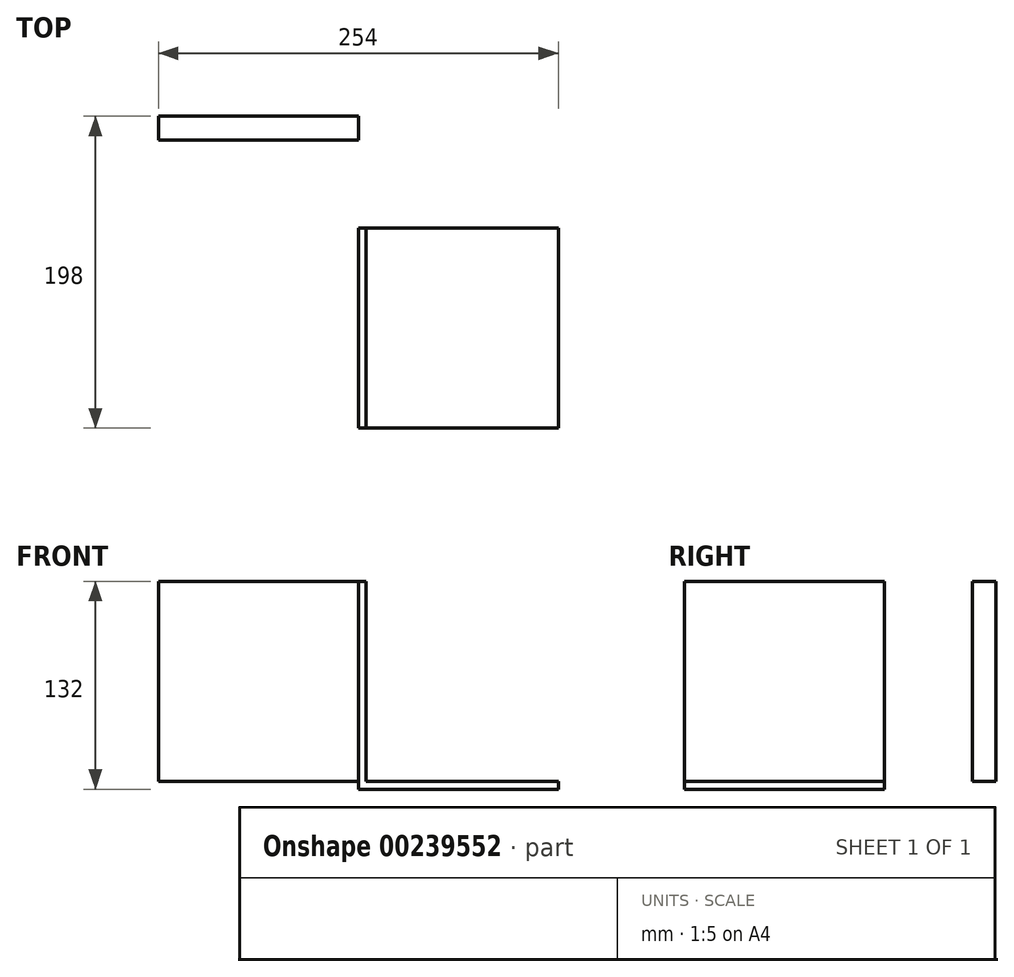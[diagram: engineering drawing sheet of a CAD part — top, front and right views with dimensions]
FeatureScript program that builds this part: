
annotation { "Feature Type Name" : "Feature", "Feature Type Description" : "" }
export const myFeature = defineFeature(function(context is Context, id is Id, definition is map)
    precondition{}
    {
        {
            assignVariable(context, id + "F0", {"name" : "L", "anyValue" : 5});
        }
        {
            var Q0;
            Q0=qCreatedBy(makeId("Front.planeOp"),FACE);
            var sketch = newSketch(context, id + "F1", { "sketchPlane" : qUnion([Q0])});
            skLineSegment(sketch, "E0.bottom", {"start": v(63.5, 63.5) * mm, "end": v(-63.5, 63.5) * mm});
            skLineSegment(sketch, "E0.top", {"start": v(63.5, -63.5) * mm, "end": v(-63.5, -63.5) * mm});
            skLineSegment(sketch, "E0.left", {"start": v(63.5, 63.5) * mm, "end": v(63.5, -63.5) * mm});
            skLineSegment(sketch, "E0.right", {"start": v(-63.5, 63.5) * mm, "end": v(-63.5, -63.5) * mm});
            skPoint(sketch, "E0.middle", {"position": v(0, 0) * mm});
            skSolve(sketch);
        }
        {
            var Q0;
            Q0 = qSketchRegion(id + "F1", true);
            extrude(context, id + "F2", {"entities" : qUnion([Q0]), "endBound" : BoundingType.SYMMETRIC, "depth" : (getVariable(context, 'L') * 3) * mm});
        }
        {
            var Q0;
            Q0=makeQuery(id+"F2.opExtrude","SWEPT_FACE",FACE,{"disambiguationData":[OSD([sQuery(id+"F1.wireOp",EDGE,"E0.left")])]});
            var sketch = newSketch(context, id + "F3", { "sketchPlane" : qUnion([Q0])});
            skLineSegment(sketch, "E1.bottom", {"start": v(-190.5, 63.5) * mm, "end": v(-63.5, 63.5) * mm});
            skLineSegment(sketch, "E1.top", {"start": v(-190.5, -63.5) * mm, "end": v(-63.5, -63.5) * mm});
            skLineSegment(sketch, "E1.left", {"start": v(-190.5, 63.5) * mm, "end": v(-190.5, -63.5) * mm});
            skLineSegment(sketch, "E1.right", {"start": v(-63.5, 63.5) * mm, "end": v(-63.5, -63.5) * mm});
            skSolve(sketch);
        }
        {
            var Q0;
            Q0 = qSketchRegion(id + "F3", true);
            extrude(context, id + "F4", {"entities" : qUnion([Q0]), "operationType" : NewBodyOperationType.ADD, "depth" : (getVariable(context, 'L')) * mm});
        }
        {
            var Q0;
            Q0=makeQuery(id+"F4.boolean.opBoolean","MERGE",FACE,{"derivedFrom":[makeQuery(id+"F2.opExtrude","SWEPT_FACE",FACE,{"disambiguationData":[OSD([sQuery(id+"F1.wireOp",EDGE,"E0.top")])]}),makeQuery(id+"F4.opExtrude","SWEPT_FACE",FACE,{"disambiguationData":[OSD([sQuery(id+"F3.wireOp",EDGE,"E1.top")])]})]});
            var sketch = newSketch(context, id + "F5", { "sketchPlane" : qUnion([Q0])});
            skLineSegment(sketch, "E2.bottom", {"start": v(63.5, 63.5) * mm, "end": v(190.5, 63.5) * mm});
            skLineSegment(sketch, "E2.top", {"start": v(63.5, 190.5) * mm, "end": v(190.5, 190.5) * mm});
            skLineSegment(sketch, "E2.left", {"start": v(63.5, 63.5) * mm, "end": v(63.5, 190.5) * mm});
            skLineSegment(sketch, "E2.right", {"start": v(190.5, 63.5) * mm, "end": v(190.5, 190.5) * mm});
            skSolve(sketch);
        }
        {
            var Q0;
            Q0 = qSketchRegion(id + "F5", true);
            extrude(context, id + "F6", {"entities" : qUnion([Q0]), "operationType" : NewBodyOperationType.ADD, "depth" : (getVariable(context, 'L')) * mm});
        }
    });
